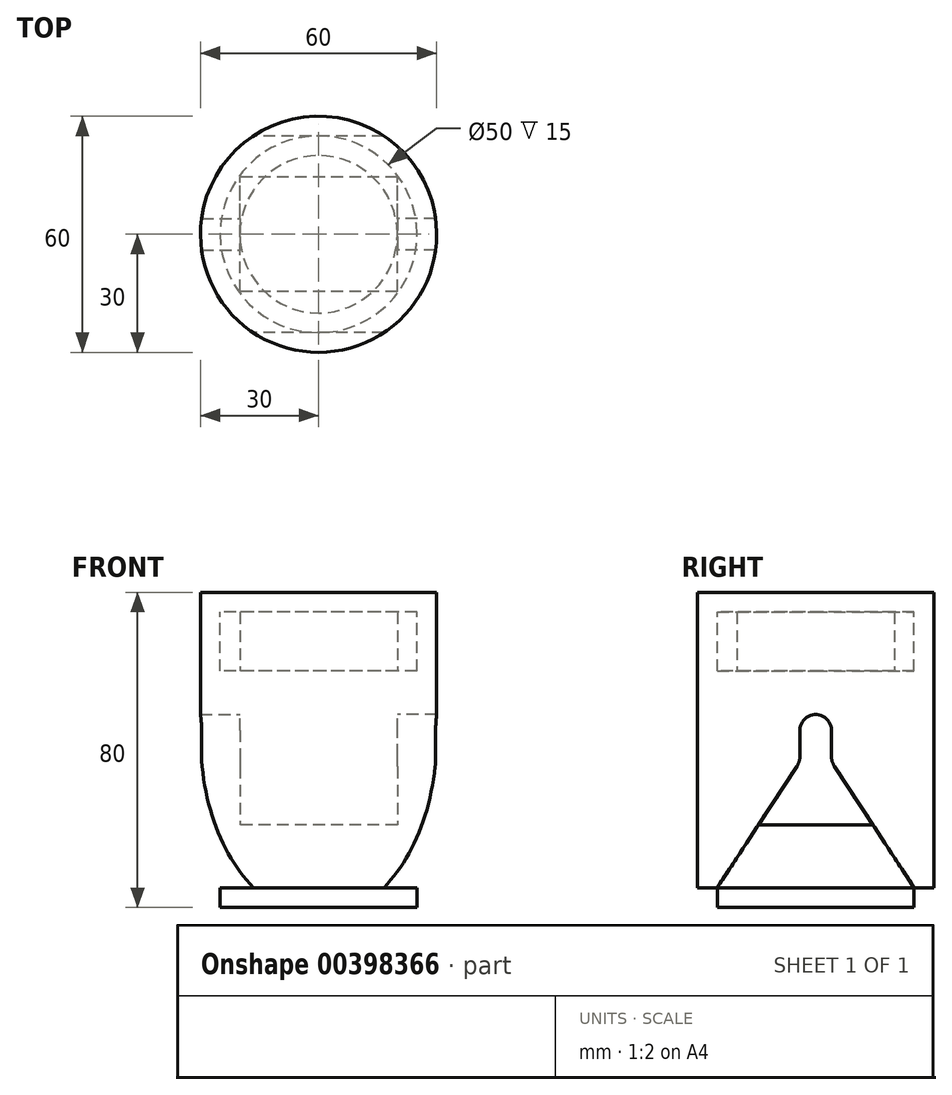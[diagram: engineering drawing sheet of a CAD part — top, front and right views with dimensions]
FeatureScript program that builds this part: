
annotation { "Feature Type Name" : "Feature", "Feature Type Description" : "" }
export const myFeature = defineFeature(function(context is Context, id is Id, definition is map)
    precondition{}
    {
        {
            var Q0;
            Q0=qCreatedBy(makeId("Top.planeOp"),FACE);
            var sketch = newSketch(context, id + "F0", { "sketchPlane" : qUnion([Q0])});
            skCircle(sketch, "E0", {"center": v(0, 0) * mm, "radius": 20 * mm});
            skCircle(sketch, "E1", {"center": v(0, 0) * mm, "radius": 25 * mm});
            skCircle(sketch, "E2", {"center": v(0, 12) * mm, "radius": 2.5 * mm});
            skCircle(sketch, "E3", {"center": v(0, 12) * mm, "radius": 3.5 * mm});
            skCircle(sketch, "E4.1.0", {"center": v(11.09, 4.6) * mm, "radius": 3.5 * mm});
            skCircle(sketch, "E4.1.1", {"center": v(11.09, 4.6) * mm, "radius": 2.5 * mm});
            skCircle(sketch, "E4.2.0", {"center": v(8.49, -8.49) * mm, "radius": 3.5 * mm});
            skCircle(sketch, "E4.2.1", {"center": v(8.49, -8.49) * mm, "radius": 2.5 * mm});
            skLineSegment(sketch, "E4.anchor1", {"start": v(0, 0) * mm, "end": v(0, 12) * mm, "construction": true});
            skLineSegment(sketch, "E4.anchor2", {"start": v(0, 0) * mm, "end": v(8.49, -8.49) * mm, "construction": true});
            skCircle(sketch, "E5.1.0", {"center": v(-11.09, 4.6) * mm, "radius": 3.5 * mm});
            skCircle(sketch, "E5.1.1", {"center": v(-11.09, 4.6) * mm, "radius": 2.5 * mm});
            skCircle(sketch, "E5.2.0", {"center": v(-8.49, -8.49) * mm, "radius": 3.5 * mm});
            skCircle(sketch, "E5.2.1", {"center": v(-8.49, -8.49) * mm, "radius": 2.5 * mm});
            skLineSegment(sketch, "E5.anchor2", {"start": v(0, 0) * mm, "end": v(-8.49, -8.49) * mm, "construction": true});
            skSolve(sketch);
        }
        {
            var Q0;
            Q0 = qSketchRegion(id + "F0", true);
            extrude(context, id + "F1", {"entities" : qUnion([Q0]), "depth" : 35 * mm});
        }
        {
            var Q0;
            Q0=makeQuery(id+"F0.imprint","IMPRINT",FACE,{"disambiguationData":[TD([[makeQuery(id+"F0.imprint","IMPRINT",EDGE,{"derivedFrom":sQuery(id+"F0.wireOp",EDGE,"E0")}),-1.0]])]});
            var Q1;
            Q1=makeQuery(id+"F0.imprint","IMPRINT",FACE,{"disambiguationData":[TD([[makeQuery(id+"F0.imprint","IMPRINT",EDGE,{"derivedFrom":sQuery(id+"F0.wireOp",EDGE,"E0")}),1.0]])]});
            var Q2;
            Q2=makeQuery(id+"F0.imprint","IMPRINT",FACE,{"disambiguationData":[TD([[makeQuery(id+"F0.imprint","IMPRINT",EDGE,{"derivedFrom":sQuery(id+"F0.wireOp",EDGE,"E5.2.0")}),1.0]])]});
            var Q3;
            Q3=makeQuery(id+"F0.imprint","IMPRINT",FACE,{"disambiguationData":[TD([[makeQuery(id+"F0.imprint","IMPRINT",EDGE,{"derivedFrom":sQuery(id+"F0.wireOp",EDGE,"E5.2.1")}),1.0]])]});
            var Q4;
            Q4=makeQuery(id+"F0.imprint","IMPRINT",FACE,{"disambiguationData":[TD([[makeQuery(id+"F0.imprint","IMPRINT",EDGE,{"derivedFrom":sQuery(id+"F0.wireOp",EDGE,"E5.1.1")}),1.0]])]});
            var Q5;
            Q5=makeQuery(id+"F0.imprint","IMPRINT",FACE,{"disambiguationData":[TD([[makeQuery(id+"F0.imprint","IMPRINT",EDGE,{"derivedFrom":sQuery(id+"F0.wireOp",EDGE,"E2")}),1.0]])]});
            var Q6;
            Q6=makeQuery(id+"F0.imprint","IMPRINT",FACE,{"disambiguationData":[TD([[makeQuery(id+"F0.imprint","IMPRINT",EDGE,{"derivedFrom":sQuery(id+"F0.wireOp",EDGE,"E4.1.0")}),1.0]])]});
            var Q7;
            Q7=makeQuery(id+"F0.imprint","IMPRINT",FACE,{"disambiguationData":[TD([[makeQuery(id+"F0.imprint","IMPRINT",EDGE,{"derivedFrom":sQuery(id+"F0.wireOp",EDGE,"E4.1.1")}),1.0]])]});
            var Q8;
            Q8=makeQuery(id+"F0.imprint","IMPRINT",FACE,{"disambiguationData":[TD([[makeQuery(id+"F0.imprint","IMPRINT",EDGE,{"derivedFrom":sQuery(id+"F0.wireOp",EDGE,"E4.2.1")}),1.0]])]});
            var Q9;
            Q9=makeQuery(id+"F0.imprint","IMPRINT",FACE,{"disambiguationData":[TD([[makeQuery(id+"F0.imprint","IMPRINT",EDGE,{"derivedFrom":sQuery(id+"F0.wireOp",EDGE,"E4.2.0")}),1.0]])]});
            var Q10;
            Q10=makeQuery(id+"F0.imprint","IMPRINT",FACE,{"disambiguationData":[TD([[makeQuery(id+"F0.imprint","IMPRINT",EDGE,{"derivedFrom":sQuery(id+"F0.wireOp",EDGE,"E5.1.0")}),1.0]])]});
            var Q11;
            Q11=makeQuery(id+"F0.imprint","IMPRINT",FACE,{"disambiguationData":[TD([[makeQuery(id+"F0.imprint","IMPRINT",EDGE,{"derivedFrom":sQuery(id+"F0.wireOp",EDGE,"E2")}),-1.0]])]});
            extrude(context, id + "F2", {"entities" : qUnion([Q0, Q1, Q2, Q3, Q4, Q5, Q6, Q7, Q8, Q9, Q10, Q11]), "operationType" : NewBodyOperationType.ADD, "oppositeDirection" : true, "depth" : 25 * mm});
        }
        {
            var Q0;
            Q0=makeQuery(id+"F0.imprint","IMPRINT",FACE,{"disambiguationData":[TD([[makeQuery(id+"F0.imprint","IMPRINT",EDGE,{"derivedFrom":sQuery(id+"F0.wireOp",EDGE,"E2")}),-1.0]])]});
            var Q1;
            Q1=makeQuery(id+"F0.imprint","IMPRINT",FACE,{"disambiguationData":[TD([[makeQuery(id+"F0.imprint","IMPRINT",EDGE,{"derivedFrom":sQuery(id+"F0.wireOp",EDGE,"E5.1.0")}),1.0]])]});
            var Q2;
            Q2=makeQuery(id+"F0.imprint","IMPRINT",FACE,{"disambiguationData":[TD([[makeQuery(id+"F0.imprint","IMPRINT",EDGE,{"derivedFrom":sQuery(id+"F0.wireOp",EDGE,"E4.1.0")}),1.0]])]});
            var Q3;
            Q3=makeQuery(id+"F0.imprint","IMPRINT",FACE,{"disambiguationData":[TD([[makeQuery(id+"F0.imprint","IMPRINT",EDGE,{"derivedFrom":sQuery(id+"F0.wireOp",EDGE,"E4.2.0")}),1.0]])]});
            var Q4;
            Q4=makeQuery(id+"F0.imprint","IMPRINT",FACE,{"disambiguationData":[TD([[makeQuery(id+"F0.imprint","IMPRINT",EDGE,{"derivedFrom":sQuery(id+"F0.wireOp",EDGE,"E5.2.0")}),1.0]])]});
            extrude(context, id + "F3", {"entities" : qUnion([Q0, Q1, Q2, Q3, Q4]), "operationType" : NewBodyOperationType.ADD, "depth" : 25 * mm});
        }
        {
            var Q0;
            Q0=qCreatedBy(makeId("Right.planeOp"),FACE);
            cPlane(context, id + "F4", {"entities" : qUnion([Q0]), "cplaneType" : CPlaneType.OFFSET, "offset" : 20 * mm, "oppositeDirection" : true, "width" : 150 * mm, "height" : 150 * mm});
        }
        {
            var Q0;
            Q0=qCreatedBy(id+"F4.planeOp",FACE);
            var sketch = newSketch(context, id + "F5", { "sketchPlane" : qUnion([Q0])});
            skCircle(sketch, "E6", {"center": v(0, 20) * mm, "radius": 4 * mm});
            skSolve(sketch);
        }
        {
            var Q0;
            Q0 = qSketchRegion(id + "F5", true);
            extrude(context, id + "F6", {"entities" : qUnion([Q0]), "operationType" : NewBodyOperationType.ADD, "oppositeDirection" : true, "depth" : 10 * mm});
        }
        {
            var Q0;
            Q0=makeQuery(id+"F1.opExtrude","SWEPT_BODY",BODY,{"disambiguationData":[OSD([sQuery(id+"F0.wireOp",EDGE,"E0"),sQuery(id+"F0.wireOp",EDGE,"E1")])]});
            var Q1;
            Q1=qCreatedBy(makeId("Right.planeOp"),FACE);
            mirror(context, id + "F7", {"operationType" : NewBodyOperationType.ADD, "entities" : qUnion([Q0]), "mirrorPlane" : qUnion([Q1])});
        }
        {
            var Q0;
            Q0=qCreatedBy(makeId("Top.planeOp"),FACE);
            var sketch = newSketch(context, id + "F8", { "sketchPlane" : qUnion([Q0])});
            skCircle(sketch, "E7", {"center": v(0, 0) * mm, "radius": 20 * mm});
            skCircle(sketch, "E8", {"center": v(11.09, 4.6) * mm, "radius": 3.5 * mm});
            skCircle(sketch, "E9", {"center": v(0, 12) * mm, "radius": 2.5 * mm});
            skCircle(sketch, "E10", {"center": v(-11.09, 4.6) * mm, "radius": 3.5 * mm});
            skCircle(sketch, "E11", {"center": v(-11.09, 4.6) * mm, "radius": 2.5 * mm});
            skCircle(sketch, "E12", {"center": v(0, 12) * mm, "radius": 3.5 * mm});
            skCircle(sketch, "E13", {"center": v(11.09, 4.6) * mm, "radius": 2.5 * mm});
            skCircle(sketch, "E14", {"center": v(8.49, -8.49) * mm, "radius": 3.5 * mm});
            skCircle(sketch, "E15", {"center": v(8.49, -8.49) * mm, "radius": 2.5 * mm});
            skCircle(sketch, "E16", {"center": v(-8.49, -8.49) * mm, "radius": 3.5 * mm});
            skCircle(sketch, "E17", {"center": v(-8.49, -8.49) * mm, "radius": 2.5 * mm});
            skSolve(sketch);
        }
        {
            var Q0;
            Q0 = qSketchRegion(id + "F8", true);
            var Q1;
            Q1=makeQuery(id+"F0.imprint","IMPRINT",FACE,{"disambiguationData":[TD([[makeQuery(id+"F0.imprint","IMPRINT",EDGE,{"derivedFrom":sQuery(id+"F0.wireOp",EDGE,"E2")}),1.0]])]});
            var Q2;
            Q2=makeQuery(id+"F0.imprint","IMPRINT",FACE,{"disambiguationData":[TD([[makeQuery(id+"F0.imprint","IMPRINT",EDGE,{"derivedFrom":sQuery(id+"F0.wireOp",EDGE,"E5.1.1")}),1.0]])]});
            var Q3;
            Q3=makeQuery(id+"F0.imprint","IMPRINT",FACE,{"disambiguationData":[TD([[makeQuery(id+"F0.imprint","IMPRINT",EDGE,{"derivedFrom":sQuery(id+"F0.wireOp",EDGE,"E5.2.1")}),1.0]])]});
            var Q4;
            Q4=makeQuery(id+"F0.imprint","IMPRINT",FACE,{"disambiguationData":[TD([[makeQuery(id+"F0.imprint","IMPRINT",EDGE,{"derivedFrom":sQuery(id+"F0.wireOp",EDGE,"E4.2.1")}),1.0]])]});
            var Q5;
            Q5=makeQuery(id+"F0.imprint","IMPRINT",FACE,{"disambiguationData":[TD([[makeQuery(id+"F0.imprint","IMPRINT",EDGE,{"derivedFrom":sQuery(id+"F0.wireOp",EDGE,"E4.1.1")}),1.0]])]});
            extrude(context, id + "F9", {"entities" : qUnion([Q0, Q1, Q2, Q3, Q4, Q5]), "depth" : 30 * mm});
        }
        {
            var Q0;
            Q0=makeQuery(id+"F1.opExtrude","CAP_FACE",FACE,{"disambiguationData":[OSD([sQuery(id+"F0.wireOp",EDGE,"E0"),sQuery(id+"F0.wireOp",EDGE,"E1")])],"isStart":false});
            var sketch = newSketch(context, id + "F10", { "sketchPlane" : qUnion([Q0])});
            skCircle(sketch, "E18", {"center": v(0, 0) * mm, "radius": 20 * mm});
            skSolve(sketch);
        }
        {
            var Q0;
            Q0 = qSketchRegion(id + "F10", true);
            extrude(context, id + "F11", {"entities" : qUnion([Q0]), "operationType" : NewBodyOperationType.ADD, "endBound" : BoundingType.SYMMETRIC, "depth" : 30 * mm});
        }
        {
            var Q0;
            Q0=makeQuery(id+"F11.opExtrude","CAP_FACE",FACE,{"disambiguationData":[OSD([sQuery(id+"F10.wireOp",EDGE,"E18")])],"isStart":false});
            var sketch = newSketch(context, id + "F12", { "sketchPlane" : qUnion([Q0])});
            skCircle(sketch, "E19", {"center": v(0, 0) * mm, "radius": 30 * mm});
            skCircle(sketch, "E20", {"center": v(0, 0) * mm, "radius": 25 * mm});
            skSolve(sketch);
        }
        {
            var Q0;
            Q0=makeQuery(id+"F12.imprint","IMPRINT",FACE,{"disambiguationData":[TD([[makeQuery(id+"F12.imprint","IMPRINT",EDGE,{"derivedFrom":sQuery(id+"F12.wireOp",EDGE,"E19")}),1.0]])]});
            var Q1;
            Q1=makeQuery(id+"F12.imprint","IMPRINT",FACE,{"disambiguationData":[TD([[makeQuery(id+"F12.imprint","IMPRINT",EDGE,{"derivedFrom":makeQuery(id+"F11.opExtrude","CAP_EDGE",EDGE,{"disambiguationData":[OSD([sQuery(id+"F10.wireOp",EDGE,"E18")])],"isStart":false})}),1.0]])]});
            var Q2;
            Q2=makeQuery(id+"F12.imprint","IMPRINT",FACE,{"disambiguationData":[TD([[makeQuery(id+"F12.imprint","IMPRINT",EDGE,{"derivedFrom":sQuery(id+"F12.wireOp",EDGE,"E20")}),1.0]])]});
            extrude(context, id + "F13", {"entities" : qUnion([Q0, Q1, Q2]), "operationType" : NewBodyOperationType.ADD, "depth" : 5 * mm});
        }
        {
            var Q0;
            Q0=makeQuery(id+"F12.imprint","IMPRINT",FACE,{"disambiguationData":[TD([[makeQuery(id+"F12.imprint","IMPRINT",EDGE,{"derivedFrom":sQuery(id+"F12.wireOp",EDGE,"E19")}),1.0]])]});
            extrude(context, id + "F14", {"entities" : qUnion([Q0]), "operationType" : NewBodyOperationType.ADD, "oppositeDirection" : true, "depth" : 70 * mm});
        }
        {
            var Q0;
            Q0=qCreatedBy(id+"F4.planeOp",FACE);
            var sketch = newSketch(context, id + "F15", { "sketchPlane" : qUnion([Q0])});
            skLineSegment(sketch, "E21", {"start": v(4, 20) * mm, "end": v(4, 13.5) * mm});
            skLineSegment(sketch, "E22", {"start": v(4.82, 10.75) * mm, "end": v(25, -20) * mm});
            skLineSegment(sketch, "E23", {"start": v(25, -20) * mm, "end": v(-25, -20) * mm});
            skLineSegment(sketch, "E24", {"start": v(-25, -20) * mm, "end": v(-4.82, 10.75) * mm});
            skLineSegment(sketch, "E25", {"start": v(-4, 13.5) * mm, "end": v(-4, 20) * mm});
            skArc(sketch, "E26", {"start": v(4, 20) * mm, "mid": v(0, 24) * mm, "end": v(-4, 20) * mm});
            skPoint(sketch, "E27.visualSharp", {"position": v(-4, 12) * mm});
            skArc(sketch, "E27.filletArc", {"start": v(-4.82, 10.75) * mm, "mid": v(-4.2, 12.06) * mm, "end": v(-4, 13.5) * mm});
            skPoint(sketch, "E28.visualSharp", {"position": v(4, 12) * mm});
            skArc(sketch, "E28.filletArc", {"start": v(4, 13.5) * mm, "mid": v(4.2, 12.06) * mm, "end": v(4.82, 10.75) * mm});
            skLineSegment(sketch, "E29", {"start": v(0, -20) * mm, "end": v(0, 20) * mm, "construction": true});
            skSolve(sketch);
        }
        {
            var Q0;
            Q0 = qSketchRegion(id + "F15", true);
            extrude(context, id + "F16", {"entities" : qUnion([Q0]), "operationType" : NewBodyOperationType.REMOVE, "oppositeDirection" : true, "depth" : 100 * mm});
        }
        {
            var Q0;
            Q0=qCreatedBy(makeId("Right.planeOp"),FACE);
            cPlane(context, id + "F17", {"entities" : qUnion([Q0]), "cplaneType" : CPlaneType.OFFSET, "offset" : 20 * mm, "width" : 150 * mm, "height" : 150 * mm});
        }
        {
            var Q0;
            Q0=qCreatedBy(id+"F17.planeOp",FACE);
            var sketch = newSketch(context, id + "F18", { "sketchPlane" : qUnion([Q0])});
            skLineSegment(sketch, "E30", {"start": v(4, 20) * mm, "end": v(4, 13.5) * mm});
            skLineSegment(sketch, "E31", {"start": v(4.82, 10.75) * mm, "end": v(25, -20) * mm});
            skLineSegment(sketch, "E32", {"start": v(25, -20) * mm, "end": v(-25, -20) * mm});
            skLineSegment(sketch, "E33", {"start": v(-25, -20) * mm, "end": v(-4.82, 10.75) * mm});
            skLineSegment(sketch, "E34", {"start": v(-4, 13.5) * mm, "end": v(-4, 20) * mm});
            skArc(sketch, "E35", {"start": v(4, 20) * mm, "mid": v(0, 24) * mm, "end": v(-4, 20) * mm});
            skPoint(sketch, "E36.visualSharp", {"position": v(-4, 12) * mm});
            skArc(sketch, "E36.filletArc", {"start": v(-4.82, 10.75) * mm, "mid": v(-4.2, 12.06) * mm, "end": v(-4, 13.5) * mm});
            skPoint(sketch, "E37.visualSharp", {"position": v(4, 12) * mm});
            skArc(sketch, "E37.filletArc", {"start": v(4, 13.5) * mm, "mid": v(4.2, 12.06) * mm, "end": v(4.82, 10.75) * mm});
            skLineSegment(sketch, "E38", {"start": v(0, -20) * mm, "end": v(0, 20) * mm, "construction": true});
            skSolve(sketch);
        }
        {
            var Q0;
            Q0 = qSketchRegion(id + "F18", true);
            extrude(context, id + "F19", {"entities" : qUnion([Q0]), "operationType" : NewBodyOperationType.REMOVE, "depth" : 25 * mm});
        }
        {
            var Q0;
            Q0=qCreatedBy(makeId("Right.planeOp"),FACE);
            var sketch = newSketch(context, id + "F20", { "sketchPlane" : qUnion([Q0])});
            skLineSegment(sketch, "E39", {"start": v(-25, -20) * mm, "end": v(25, -20) * mm});
            skLineSegment(sketch, "E40", {"start": v(25, -20) * mm, "end": v(14.5, -4) * mm});
            skLineSegment(sketch, "E41", {"start": v(14.5, -4) * mm, "end": v(-14.5, -4) * mm});
            skLineSegment(sketch, "E42", {"start": v(-14.5, -4) * mm, "end": v(-25, -20) * mm});
            skSolve(sketch);
        }
        {
            var Q0;
            Q0 = qSketchRegion(id + "F20", true);
            extrude(context, id + "F21", {"entities" : qUnion([Q0]), "operationType" : NewBodyOperationType.REMOVE, "endBound" : BoundingType.SYMMETRIC, "depth" : 60 * mm});
        }
    });
